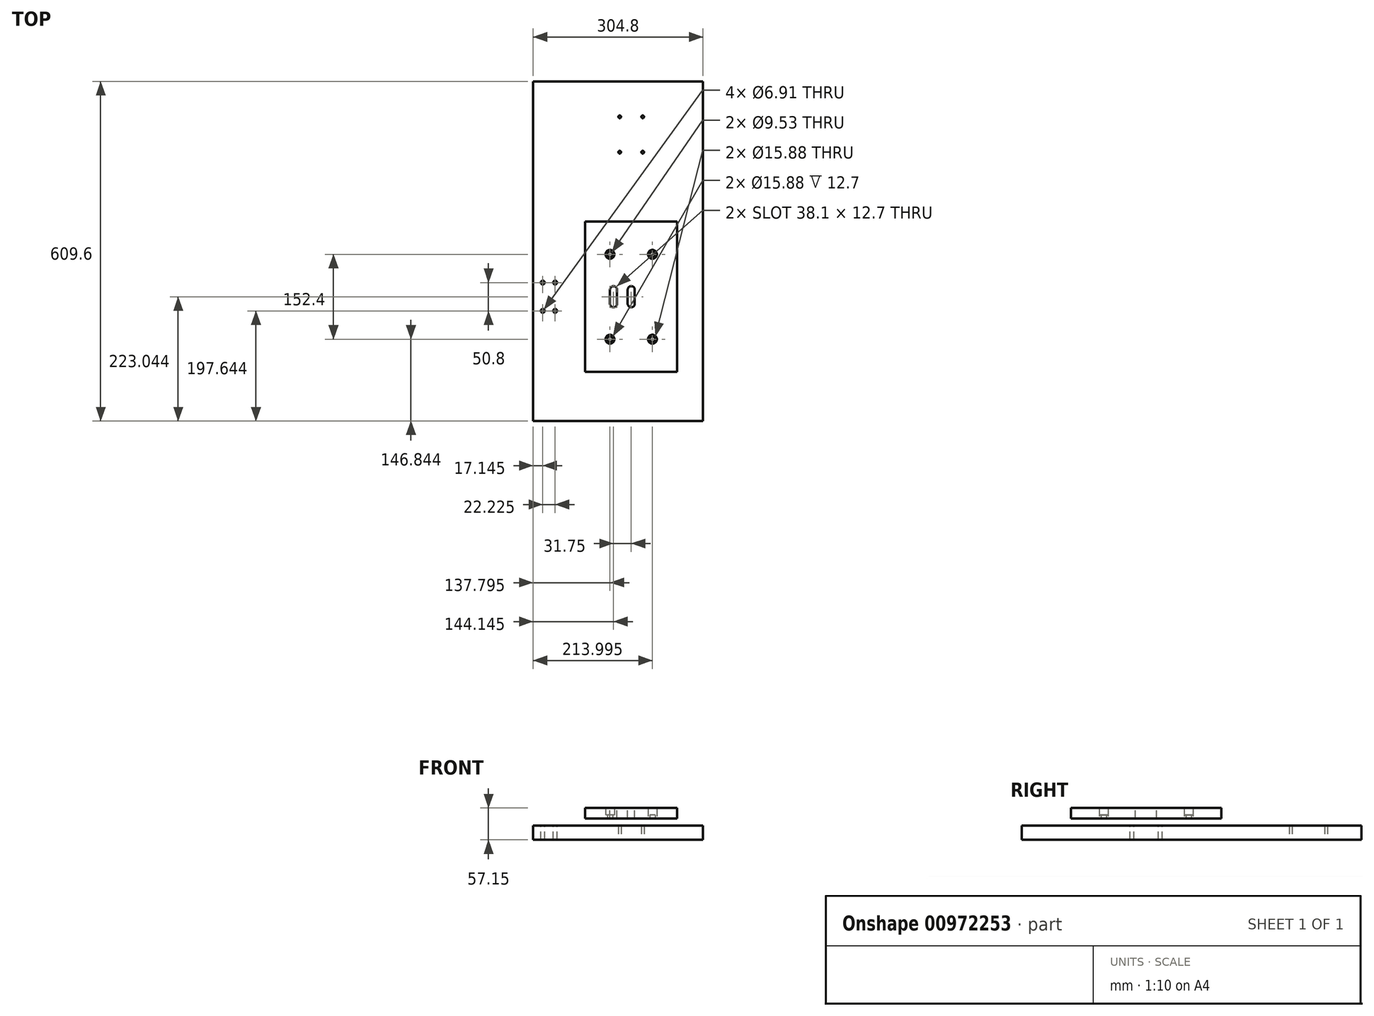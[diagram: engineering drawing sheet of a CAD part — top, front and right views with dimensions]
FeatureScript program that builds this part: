
annotation { "Feature Type Name" : "Feature", "Feature Type Description" : "" }
export const myFeature = defineFeature(function(context is Context, id is Id, definition is map)
    precondition{}
    {
        {
            var Q0;
            Q0=qCreatedBy(makeId("Top.planeOp"),FACE);
            var sketch = newSketch(context, id + "F0", { "sketchPlane" : qUnion([Q0])});
            skLineSegment(sketch, "E0.bottom", {"start": v(-152.4, 0) * mm, "end": v(152.4, 0) * mm});
            skLineSegment(sketch, "E0.top", {"start": v(-152.4, -609.6) * mm, "end": v(152.4, -609.6) * mm});
            skLineSegment(sketch, "E0.left", {"start": v(-152.4, 0) * mm, "end": v(-152.4, -609.6) * mm});
            skLineSegment(sketch, "E0.right", {"start": v(152.4, 0) * mm, "end": v(152.4, -609.6) * mm});
            skLineSegment(sketch, "E1", {"start": v(23.5, 0) * mm, "end": v(23.5, -609.6) * mm, "construction": true});
            skCircle(sketch, "E2", {"center": v(2.86, -63.5) * mm, "radius": 2.38 * mm});
            skCircle(sketch, "E3", {"center": v(2.86, -127) * mm, "radius": 2.38 * mm});
            skCircle(sketch, "E4.MirrorC", {"center": v(44.13, -63.5) * mm, "radius": 2.38 * mm});
            skCircle(sketch, "E5.MirrorC", {"center": v(44.13, -127) * mm, "radius": 2.38 * mm});
            skSolve(sketch);
        }
        {
            var Q0;
            Q0=makeQuery(id+"F0.imprint","IMPRINT",FACE,{"disambiguationData":[TD([[makeQuery(id+"F0.imprint","IMPRINT",EDGE,{"derivedFrom":sQuery(id+"F0.wireOp",EDGE,"E0.bottom")}),-1.0]])]});
            extrude(context, id + "F1", {"entities" : qUnion([Q0]), "depth" : 25.4 * mm, "offsetDistance" : 25.4 * mm});
        }
        {
            var Q0;
            Q0=makeQuery(id+"F1.opExtrude","CAP_FACE",FACE,{"disambiguationData":[OSD([sQuery(id+"F0.wireOp",EDGE,"E0.bottom"),sQuery(id+"F0.wireOp",EDGE,"E0.top"),sQuery(id+"F0.wireOp",EDGE,"E0.left"),sQuery(id+"F0.wireOp",EDGE,"E0.right"),sQuery(id+"F0.wireOp",EDGE,"E2"),sQuery(id+"F0.wireOp",EDGE,"E3"),sQuery(id+"F0.wireOp",EDGE,"E4.MirrorC"),sQuery(id+"F0.wireOp",EDGE,"E5.MirrorC")])],"isStart":false});
            var sketch = newSketch(context, id + "F2", { "sketchPlane" : qUnion([Q0])});
            skLineSegment(sketch, "E6.bottom", {"start": v(-40, -170.66) * mm, "end": v(87, -170.66) * mm, "construction": true});
            skLineSegment(sketch, "E6.top", {"start": v(-40, -602.46) * mm, "end": v(87, -602.46) * mm, "construction": true});
            skLineSegment(sketch, "E6.left", {"start": v(-40, -170.66) * mm, "end": v(-40, -602.46) * mm, "construction": true});
            skLineSegment(sketch, "E6.right", {"start": v(87, -170.66) * mm, "end": v(87, -602.46) * mm, "construction": true});
            skLineSegment(sketch, "E7", {"start": v(23.5, -170.66) * mm, "end": v(23.5, -602.46) * mm, "construction": true});
            skCircle(sketch, "E8", {"center": v(-14.6, -310.36) * mm, "radius": 4.76 * mm});
            skCircle(sketch, "E9", {"center": v(-14.6, -462.76) * mm, "radius": 4.76 * mm});
            skCircle(sketch, "E10.MirrorC", {"center": v(61.6, -310.36) * mm, "radius": 4.76 * mm});
            skCircle(sketch, "E11.MirrorC", {"center": v(61.6, -462.76) * mm, "radius": 4.76 * mm});
            skLineSegment(sketch, "E12", {"start": v(-14.6, -310.36) * mm, "end": v(-14.6, -462.76) * mm, "construction": true});
            skLineSegment(sketch, "E13.bottom", {"start": v(-135.25, -361.16) * mm, "end": v(-113.03, -361.16) * mm, "construction": true});
            skLineSegment(sketch, "E13.top", {"start": v(-135.25, -411.96) * mm, "end": v(-113.03, -411.96) * mm, "construction": true});
            skLineSegment(sketch, "E13.left", {"start": v(-135.25, -361.16) * mm, "end": v(-135.25, -411.96) * mm, "construction": true});
            skLineSegment(sketch, "E13.right", {"start": v(-113.03, -361.16) * mm, "end": v(-113.03, -411.96) * mm, "construction": true});
            skLineSegment(sketch, "E14", {"start": v(-113.03, -386.56) * mm, "end": v(23.5, -386.56) * mm, "construction": true});
            skCircle(sketch, "E15.0", {"center": v(2.86, -127) * mm, "radius": 2.38 * mm, "construction": true});
            skCircle(sketch, "E16.0", {"center": v(44.13, -127) * mm, "radius": 2.38 * mm, "construction": true});
            skLineSegment(sketch, "E17", {"start": v(2.86, -127) * mm, "end": v(44.13, -127) * mm, "construction": true});
            skLineSegment(sketch, "E18", {"start": v(23.5, -127) * mm, "end": v(23.5, -170.66) * mm, "construction": true});
            skCircle(sketch, "E19", {"center": v(-113.03, -411.96) * mm, "radius": 3.45 * mm});
            skCircle(sketch, "E20", {"center": v(-135.25, -411.96) * mm, "radius": 3.45 * mm});
            skCircle(sketch, "E21", {"center": v(-135.25, -361.16) * mm, "radius": 3.45 * mm});
            skCircle(sketch, "E22", {"center": v(-113.03, -361.16) * mm, "radius": 3.45 * mm});
            skLineSegment(sketch, "E23.bottom", {"start": v(-59.05, -251.62) * mm, "end": v(106.05, -251.62) * mm});
            skLineSegment(sketch, "E23.top", {"start": v(-59.05, -521.5) * mm, "end": v(106.05, -521.5) * mm});
            skLineSegment(sketch, "E23.left", {"start": v(-59.05, -251.62) * mm, "end": v(-59.05, -521.5) * mm});
            skLineSegment(sketch, "E23.right", {"start": v(106.05, -251.62) * mm, "end": v(106.05, -521.5) * mm});
            skLineSegment(sketch, "E24", {"start": v(-59.05, -251.62) * mm, "end": v(106.05, -521.5) * mm, "construction": true});
            skCircle(sketch, "E25", {"center": v(-14.6, -310.36) * mm, "radius": 7.94 * mm});
            skCircle(sketch, "E26", {"center": v(61.6, -310.36) * mm, "radius": 7.94 * mm});
            skCircle(sketch, "E27", {"center": v(61.6, -462.76) * mm, "radius": 7.94 * mm});
            skCircle(sketch, "E28", {"center": v(-14.6, -462.76) * mm, "radius": 7.94 * mm});
            skSolve(sketch);
        }
        {
            var Q0;
            Q0=makeQuery(id+"F2.imprint","IMPRINT",FACE,{"disambiguationData":[TD([[makeQuery(id+"F2.imprint","IMPRINT",EDGE,{"derivedFrom":sQuery(id+"F2.wireOp",EDGE,"E21")}),1.0]])]});
            var Q1;
            Q1=makeQuery(id+"F2.imprint","IMPRINT",FACE,{"disambiguationData":[TD([[makeQuery(id+"F2.imprint","IMPRINT",EDGE,{"derivedFrom":sQuery(id+"F2.wireOp",EDGE,"E22")}),1.0]])]});
            var Q2;
            Q2=makeQuery(id+"F2.imprint","IMPRINT",FACE,{"disambiguationData":[TD([[makeQuery(id+"F2.imprint","IMPRINT",EDGE,{"derivedFrom":sQuery(id+"F2.wireOp",EDGE,"E19")}),1.0]])]});
            var Q3;
            Q3=makeQuery(id+"F2.imprint","IMPRINT",FACE,{"disambiguationData":[TD([[makeQuery(id+"F2.imprint","IMPRINT",EDGE,{"derivedFrom":sQuery(id+"F2.wireOp",EDGE,"E20")}),1.0]])]});
            extrude(context, id + "F3", {"entities" : qUnion([Q0, Q1, Q2, Q3]), "operationType" : NewBodyOperationType.REMOVE, "oppositeDirection" : true, "depth" : 25.4 * mm, "offsetDistance" : 25.4 * mm});
        }
        {
            var Q0;
            Q0=makeQuery(id+"F2.imprint","IMPRINT",FACE,{"disambiguationData":[TD([[makeQuery(id+"F2.imprint","IMPRINT",EDGE,{"derivedFrom":sQuery(id+"F2.wireOp",EDGE,"E23.bottom")}),-1.0]])]});
            var Q1;
            Q1=makeQuery(id+"F2.imprint","IMPRINT",FACE,{"disambiguationData":[TD([[makeQuery(id+"F2.imprint","IMPRINT",EDGE,{"derivedFrom":sQuery(id+"F2.wireOp",EDGE,"E8")}),-1.0]])]});
            var Q2;
            Q2=makeQuery(id+"F2.imprint","IMPRINT",FACE,{"disambiguationData":[TD([[makeQuery(id+"F2.imprint","IMPRINT",EDGE,{"derivedFrom":sQuery(id+"F2.wireOp",EDGE,"E10.MirrorC")}),1.0]])]});
            var Q3;
            Q3=makeQuery(id+"F2.imprint","IMPRINT",FACE,{"disambiguationData":[TD([[makeQuery(id+"F2.imprint","IMPRINT",EDGE,{"derivedFrom":sQuery(id+"F2.wireOp",EDGE,"E9")}),-1.0]])]});
            var Q4;
            Q4=makeQuery(id+"F2.imprint","IMPRINT",FACE,{"disambiguationData":[TD([[makeQuery(id+"F2.imprint","IMPRINT",EDGE,{"derivedFrom":sQuery(id+"F2.wireOp",EDGE,"E11.MirrorC")}),1.0]])]});
            extrude(context, id + "F4", {"entities" : qUnion([Q0, Q1, Q2, Q3, Q4]), "depth" : 31.75 * mm, "offsetDistance" : 25.4 * mm, "hasSecondDirection" : true, "secondDirectionOppositeDirection" : false, "secondDirectionDepth" : 12.7 * mm});
        }
        {
            var Q0;
            Q0=makeQuery(id+"F2.imprint","IMPRINT",FACE,{"disambiguationData":[TD([[makeQuery(id+"F2.imprint","IMPRINT",EDGE,{"derivedFrom":sQuery(id+"F2.wireOp",EDGE,"E8")}),-1.0]])]});
            var Q1;
            Q1=makeQuery(id+"F2.imprint","IMPRINT",FACE,{"disambiguationData":[TD([[makeQuery(id+"F2.imprint","IMPRINT",EDGE,{"derivedFrom":sQuery(id+"F2.wireOp",EDGE,"E8")}),1.0]])]});
            var Q2;
            Q2=makeQuery(id+"F2.imprint","IMPRINT",FACE,{"disambiguationData":[TD([[makeQuery(id+"F2.imprint","IMPRINT",EDGE,{"derivedFrom":sQuery(id+"F2.wireOp",EDGE,"E10.MirrorC")}),1.0]])]});
            var Q3;
            Q3=makeQuery(id+"F2.imprint","IMPRINT",FACE,{"disambiguationData":[TD([[makeQuery(id+"F2.imprint","IMPRINT",EDGE,{"derivedFrom":sQuery(id+"F2.wireOp",EDGE,"E10.MirrorC")}),-1.0]])]});
            var Q4;
            Q4=makeQuery(id+"F2.imprint","IMPRINT",FACE,{"disambiguationData":[TD([[makeQuery(id+"F2.imprint","IMPRINT",EDGE,{"derivedFrom":sQuery(id+"F2.wireOp",EDGE,"E9")}),-1.0]])]});
            var Q5;
            Q5=makeQuery(id+"F2.imprint","IMPRINT",FACE,{"disambiguationData":[TD([[makeQuery(id+"F2.imprint","IMPRINT",EDGE,{"derivedFrom":sQuery(id+"F2.wireOp",EDGE,"E9")}),1.0]])]});
            var Q6;
            Q6=makeQuery(id+"F2.imprint","IMPRINT",FACE,{"disambiguationData":[TD([[makeQuery(id+"F2.imprint","IMPRINT",EDGE,{"derivedFrom":sQuery(id+"F2.wireOp",EDGE,"E11.MirrorC")}),1.0]])]});
            var Q7;
            Q7=makeQuery(id+"F2.imprint","IMPRINT",FACE,{"disambiguationData":[TD([[makeQuery(id+"F2.imprint","IMPRINT",EDGE,{"derivedFrom":sQuery(id+"F2.wireOp",EDGE,"E11.MirrorC")}),-1.0]])]});
            extrude(context, id + "F5", {"entities" : qUnion([Q0, Q1, Q2, Q3, Q4, Q5, Q6, Q7]), "operationType" : NewBodyOperationType.REMOVE, "depth" : 254 * mm, "offsetDistance" : 25.4 * mm, "hasSecondDirection" : true, "secondDirectionOppositeDirection" : false, "secondDirectionDepth" : 19.05 * mm});
        }
        {
            var Q0;
            Q0=makeQuery(id+"F4.opExtrude","CAP_FACE",FACE,{"disambiguationData":[OSD([sQuery(id+"F2.wireOp",EDGE,"E8"),sQuery(id+"F2.wireOp",EDGE,"E9"),sQuery(id+"F2.wireOp",EDGE,"E10.MirrorC"),sQuery(id+"F2.wireOp",EDGE,"E11.MirrorC"),sQuery(id+"F2.wireOp",EDGE,"E23.bottom"),sQuery(id+"F2.wireOp",EDGE,"E23.top"),sQuery(id+"F2.wireOp",EDGE,"E23.left"),sQuery(id+"F2.wireOp",EDGE,"E23.right")])],"isStart":false});
            var sketch = newSketch(context, id + "F6", { "sketchPlane" : qUnion([Q0])});
            skLineSegment(sketch, "E29.0.0", {"start": v(-59.05, -251.62) * mm, "end": v(-59.05, -521.5) * mm, "construction": true});
            skLineSegment(sketch, "E29.0.1", {"start": v(-59.05, -521.5) * mm, "end": v(106.05, -521.5) * mm, "construction": true});
            skLineSegment(sketch, "E29.0.2", {"start": v(106.05, -521.5) * mm, "end": v(106.05, -251.62) * mm, "construction": true});
            skLineSegment(sketch, "E29.0.3", {"start": v(106.05, -251.62) * mm, "end": v(-59.05, -251.62) * mm, "construction": true});
            skLineSegment(sketch, "E30", {"start": v(-59.05, -386.56) * mm, "end": v(106.05, -386.56) * mm, "construction": true});
            skArc(sketch, "E31", {"start": v(-1.9, -373.86) * mm, "mid": v(-8.25, -367.5) * mm, "end": v(-14.6, -373.86) * mm});
            skArc(sketch, "E32", {"start": v(29.85, -373.86) * mm, "mid": v(23.5, -367.5) * mm, "end": v(17.15, -373.86) * mm});
            skArc(sketch, "E33.MirrorC", {"start": v(-1.9, -399.26) * mm, "mid": v(-8.25, -405.6) * mm, "end": v(-14.6, -399.26) * mm});
            skArc(sketch, "E34.MirrorC", {"start": v(29.85, -399.26) * mm, "mid": v(23.5, -405.6) * mm, "end": v(17.15, -399.26) * mm});
            skLineSegment(sketch, "E35", {"start": v(-14.6, -373.86) * mm, "end": v(-14.6, -399.26) * mm});
            skLineSegment(sketch, "E36", {"start": v(-1.9, -373.86) * mm, "end": v(-1.9, -399.26) * mm});
            skLineSegment(sketch, "E37", {"start": v(17.15, -373.86) * mm, "end": v(17.15, -399.26) * mm});
            skLineSegment(sketch, "E38", {"start": v(29.85, -373.86) * mm, "end": v(29.85, -399.26) * mm});
            skSolve(sketch);
        }
        {
            var Q0;
            Q0=makeQuery(id+"F6.imprint","IMPRINT",FACE,{"disambiguationData":[TD([[makeQuery(id+"F6.imprint","IMPRINT",EDGE,{"derivedFrom":sQuery(id+"F6.wireOp",EDGE,"E31")}),1.0]])]});
            var Q1;
            Q1=makeQuery(id+"F6.imprint","IMPRINT",FACE,{"disambiguationData":[TD([[makeQuery(id+"F6.imprint","IMPRINT",EDGE,{"derivedFrom":sQuery(id+"F6.wireOp",EDGE,"E32")}),1.0]])]});
            extrude(context, id + "F7", {"entities" : qUnion([Q0, Q1]), "operationType" : NewBodyOperationType.REMOVE, "oppositeDirection" : true, "depth" : 25.4 * mm, "offsetDistance" : 25.4 * mm});
        }
    });
